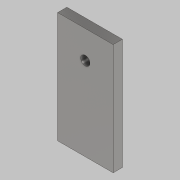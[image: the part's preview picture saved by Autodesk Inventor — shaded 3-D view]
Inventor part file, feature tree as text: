
AUTODESK INVENTOR PART (.ipt)
format: ipt  version: 2021 (Build 250183000, 183)  size: 102,400 bytes
history: native  units: mm
features: sketch x2, hole x1
ambient origin geometry x8: Origin, YZ Plane, XZ Plane, XY Plane, X Axis, Y Axis, Z Axis, Center Point
bodies: Solid1 (feature_tree)
feature tree (3):
  hole  "Hole1"  [1 undecoded]
  sketch  "Sketch1"  dims[d0=30.0mm d1=15.0mm]
  sketch  "Sketch2"  dims[d2=60.0mm d3=30.0mm d4=5.0mm d5=0.0mm d6=45.0mm d7=5.0mm d8=6.0mm d9=4.0mm d10=2.0mm d11=90.0deg d12=8.0mm d13=20.594885mm]
note: 1 required parameter value undecoded (feature->parameter linkage not recoverable at this tier; creation-order binding heuristic only, values carry confidence <= 0.55)
